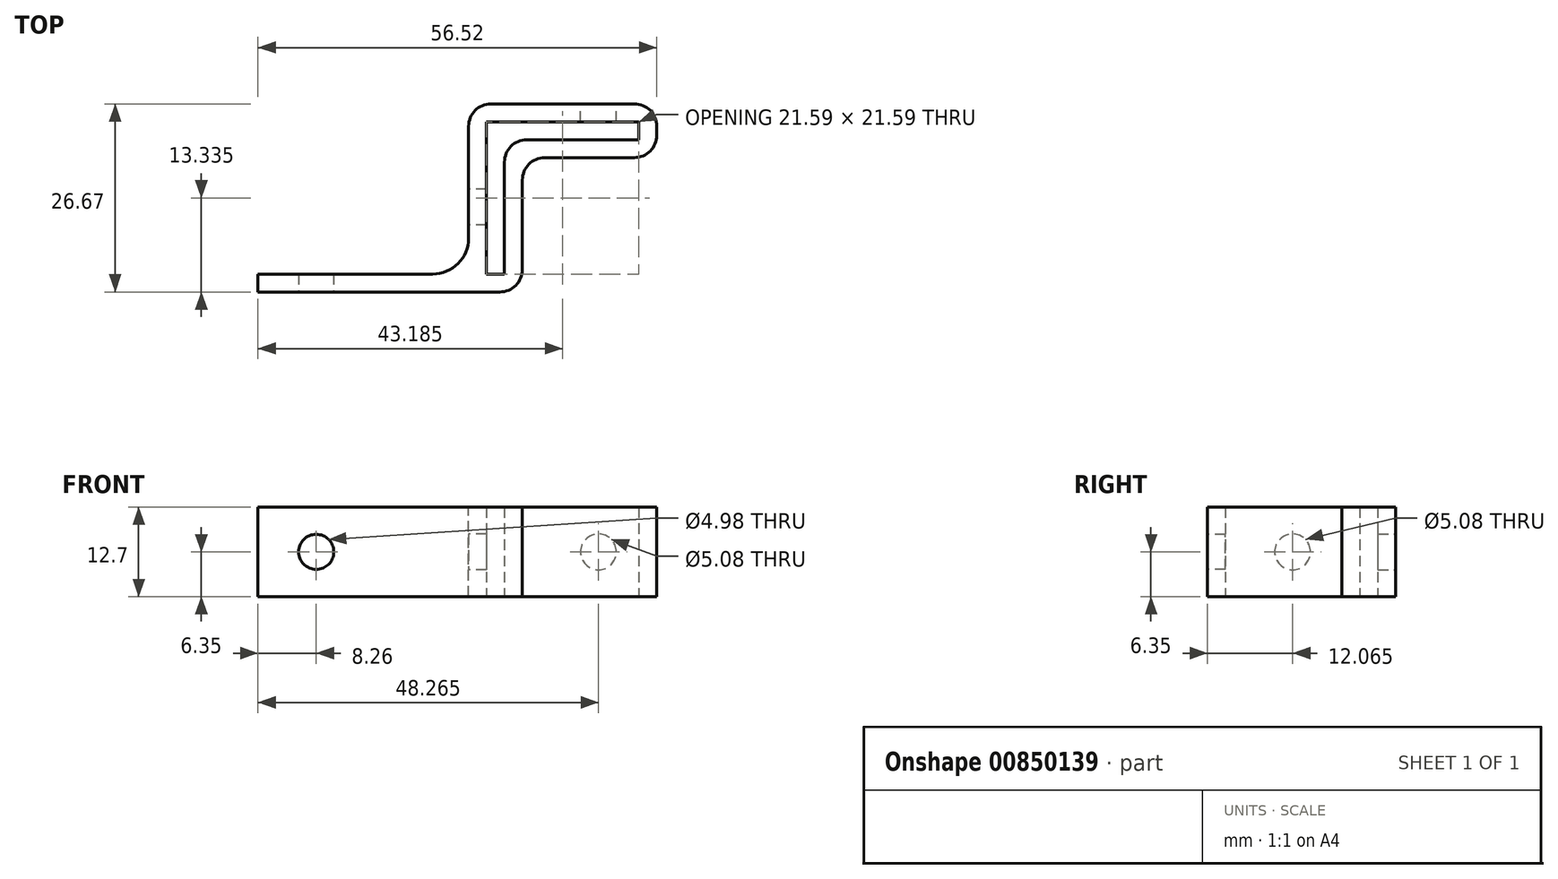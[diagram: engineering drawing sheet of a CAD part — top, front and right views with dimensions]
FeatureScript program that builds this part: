
annotation { "Feature Type Name" : "Feature", "Feature Type Description" : "" }
export const myFeature = defineFeature(function(context is Context, id is Id, definition is map)
    precondition{}
    {
        {
            var Q0;
            Q0=qCreatedBy(makeId("Top.planeOp"),FACE);
            var sketch = newSketch(context, id + "F0", { "sketchPlane" : qUnion([Q0])});
            skLineSegment(sketch, "E0.bottom", {"start": v(2.54, 0) * mm, "end": v(5.08, 0) * mm});
            skLineSegment(sketch, "E0.top", {"start": v(2.54, 21.6) * mm, "end": v(5.08, 21.6) * mm});
            skLineSegment(sketch, "E0.left", {"start": v(2.54, 0) * mm, "end": v(2.54, 21.59) * mm});
            skLineSegment(sketch, "E0.right", {"start": v(5.08, 0) * mm, "end": v(5.08, 19.05) * mm});
            skLineSegment(sketch, "E1.bottom", {"start": v(5.08, 21.6) * mm, "end": v(24.13, 21.6) * mm});
            skLineSegment(sketch, "E1.top", {"start": v(5.08, 19.05) * mm, "end": v(24.13, 19.05) * mm});
            skLineSegment(sketch, "E1.right", {"start": v(24.13, 21.6) * mm, "end": v(24.13, 19.05) * mm});
            skLineSegment(sketch, "E2", {"start": v(0, -2.2) * mm, "end": v(0, 24.13) * mm});
            skLineSegment(sketch, "E3", {"start": v(0, 24.13) * mm, "end": v(26.67, 24.13) * mm});
            skLineSegment(sketch, "E4", {"start": v(26.67, 24.13) * mm, "end": v(26.67, 16.51) * mm});
            skLineSegment(sketch, "E5", {"start": v(26.67, 16.51) * mm, "end": v(7.62, 16.5) * mm});
            skLineSegment(sketch, "E6", {"start": v(7.62, 16.5) * mm, "end": v(7.62, -2.54) * mm});
            skLineSegment(sketch, "E7", {"start": v(7.62, -2.54) * mm, "end": v(0, -2.54) * mm});
            skLineSegment(sketch, "E8", {"start": v(0, -2.54) * mm, "end": v(0, -2.2) * mm});
            skSolve(sketch);
        }
        {
            var Q0;
            Q0=qSketchRegion(id+"F0",true);
            extrude(context, id + "F1", {"entities" : qUnion([Q0]), "depth" : 12.7 * mm, "offsetDistance" : 25.4 * mm});
        }
        {
            var Q0;
            Q0=makeQuery(id+"F1.opExtrude","SWEPT_EDGE",EDGE,{"disambiguationData":[OSD([sQuery(id+"F0.wireOp",EDGE,"E3"),sQuery(id+"F0.wireOp",EDGE,"E4")])]});
            var Q1;
            Q1=makeQuery(id+"F1.opExtrude","SWEPT_EDGE",EDGE,{"disambiguationData":[OSD([sQuery(id+"F0.wireOp",EDGE,"E4"),sQuery(id+"F0.wireOp",EDGE,"E5")])]});
            var Q2;
            Q2=makeQuery(id+"F1.opExtrude","SWEPT_EDGE",EDGE,{"disambiguationData":[OSD([sQuery(id+"F0.wireOp",EDGE,"E0.right"),sQuery(id+"F0.wireOp",EDGE,"E1.top")])]});
            var Q3;
            Q3=makeQuery(id+"F1.opExtrude","SWEPT_EDGE",EDGE,{"disambiguationData":[OSD([sQuery(id+"F0.wireOp",EDGE,"E2"),sQuery(id+"F0.wireOp",EDGE,"E3")])]});
            var Q4;
            Q4=makeQuery(id+"F1.opExtrude","SWEPT_EDGE",EDGE,{"disambiguationData":[OSD([sQuery(id+"F0.wireOp",EDGE,"E6"),sQuery(id+"F0.wireOp",EDGE,"E7")])]});
            var Q5;
            Q5=makeQuery(id+"F1.opExtrude","SWEPT_EDGE",EDGE,{"disambiguationData":[OSD([sQuery(id+"F0.wireOp",EDGE,"E7"),sQuery(id+"F0.wireOp",EDGE,"E8")])]});
            var Q6;
            Q6=makeQuery(id+"F1.opExtrude","SWEPT_EDGE",EDGE,{"disambiguationData":[OSD([sQuery(id+"F0.wireOp",EDGE,"E5"),sQuery(id+"F0.wireOp",EDGE,"E6")])]});
            fillet(context, id + "F2", {"entities" : qUnion([Q0, Q1, Q2, Q3, Q4, Q5, Q6]), "radius" : 3.17 * mm, "tangentPropagation" : true, "allowEdgeOverflow" : false});
        }
        {
            var Q0;
            Q0=makeQuery(id+"F1.opExtrude","SWEPT_FACE",FACE,{"disambiguationData":[OSD([sQuery(id+"F0.wireOp",EDGE,"E7")])]});
            var sketch = newSketch(context, id + "F3", { "sketchPlane" : qUnion([Q0])});
            skLineSegment(sketch, "E9.bottom", {"start": v(3.17, 12.7) * mm, "end": v(-29.85, 12.7) * mm});
            skLineSegment(sketch, "E9.top", {"start": v(3.17, 0) * mm, "end": v(-29.85, 0) * mm});
            skLineSegment(sketch, "E9.left", {"start": v(3.17, 12.7) * mm, "end": v(3.17, 0) * mm});
            skLineSegment(sketch, "E9.right", {"start": v(-29.85, 12.7) * mm, "end": v(-29.85, 0) * mm});
            skSolve(sketch);
        }
        {
            var Q0;
            Q0 = qSketchRegion(id + "F3", true);
            extrude(context, id + "F4", {"entities" : qUnion([Q0]), "operationType" : NewBodyOperationType.ADD, "oppositeDirection" : true, "depth" : 2.54 * mm, "offsetDistance" : 25.4 * mm});
        }
        {
            var Q0;
            Q0=makeQuery(id+"F4.boolean.opBoolean","INTERSECT",EDGE,{"derivedFrom":[makeQuery(id+"F2.opFillet","BLEND_FACE",FACE,{"disambiguationData":[OSD([sQuery(id+"F0.wireOp",EDGE,"E7"),sQuery(id+"F0.wireOp",EDGE,"E8")])]}),makeQuery(id+"F4.opExtrude","CAP_FACE",FACE,{"disambiguationData":[OSD([sQuery(id+"F3.wireOp",EDGE,"E9.bottom"),sQuery(id+"F3.wireOp",EDGE,"E9.top"),sQuery(id+"F3.wireOp",EDGE,"E9.left"),sQuery(id+"F3.wireOp",EDGE,"E9.right")])],"isStart":false})]});
            fillet(context, id + "F5", {"entities" : qUnion([Q0]), "radius" : 5.08 * mm, "tangentPropagation" : true, "allowEdgeOverflow" : false});
        }
        {
            var Q0;
            Q0=makeQuery(id+"F4.boolean.opBoolean","MERGE",FACE,{"derivedFrom":[makeQuery(id+"F1.opExtrude","SWEPT_FACE",FACE,{"disambiguationData":[OSD([sQuery(id+"F0.wireOp",EDGE,"E7")])]}),makeQuery(id+"F4.opExtrude","CAP_FACE",FACE,{"disambiguationData":[OSD([sQuery(id+"F3.wireOp",EDGE,"E9.bottom"),sQuery(id+"F3.wireOp",EDGE,"E9.top"),sQuery(id+"F3.wireOp",EDGE,"E9.left"),sQuery(id+"F3.wireOp",EDGE,"E9.right")])],"isStart":true})]});
            var sketch = newSketch(context, id + "F6", { "sketchPlane" : qUnion([Q0])});
            skCircle(sketch, "E10", {"center": v(-21.59, 6.35) * mm, "radius": 2.49 * mm});
            skPoint(sketch, "E10.centerSnap0", {"position": v(-29.85, 6.35) * mm});
            skSolve(sketch);
        }
        {
            var Q0;
            Q0 = qSketchRegion(id + "F6", true);
            extrude(context, id + "F7", {"entities" : qUnion([Q0]), "operationType" : NewBodyOperationType.REMOVE, "endBound" : BoundingType.UP_TO_NEXT, "oppositeDirection" : true, "depth" : 25.4 * mm, "offsetDistance" : 25.4 * mm});
        }
        {
            var Q0;
            Q0=makeQuery(id+"F1.opExtrude","SWEPT_FACE",FACE,{"disambiguationData":[OSD([sQuery(id+"F0.wireOp",EDGE,"E3")])]});
            var sketch = newSketch(context, id + "F8", { "sketchPlane" : qUnion([Q0])});
            skCircle(sketch, "E11", {"center": v(-18.41, 6.35) * mm, "radius": 2.54 * mm});
            skPoint(sketch, "E11.centerSnap0", {"position": v(-23.5, 6.35) * mm});
            skSolve(sketch);
        }
        {
            var Q0;
            Q0 = qSketchRegion(id + "F8", true);
            extrude(context, id + "F9", {"entities" : qUnion([Q0]), "operationType" : NewBodyOperationType.REMOVE, "endBound" : BoundingType.UP_TO_NEXT, "oppositeDirection" : true, "depth" : 25.4 * mm, "offsetDistance" : 25.4 * mm});
        }
        {
            var Q0;
            Q0=makeQuery(id+"F1.opExtrude","SWEPT_FACE",FACE,{"disambiguationData":[OSD([sQuery(id+"F0.wireOp",EDGE,"E2"),sQuery(id+"F0.wireOp",EDGE,"E8")])]});
            var sketch = newSketch(context, id + "F10", { "sketchPlane" : qUnion([Q0])});
            skCircle(sketch, "E12", {"center": v(-9.53, 6.35) * mm, "radius": 2.54 * mm});
            skPoint(sketch, "E12.centerSnap0", {"position": v(-20.96, 6.35) * mm});
            skSolve(sketch);
        }
        {
            var Q0;
            Q0 = qSketchRegion(id + "F10", true);
            extrude(context, id + "F11", {"entities" : qUnion([Q0]), "operationType" : NewBodyOperationType.REMOVE, "endBound" : BoundingType.UP_TO_NEXT, "oppositeDirection" : true, "depth" : 25.4 * mm, "offsetDistance" : 25.4 * mm});
        }
    });
